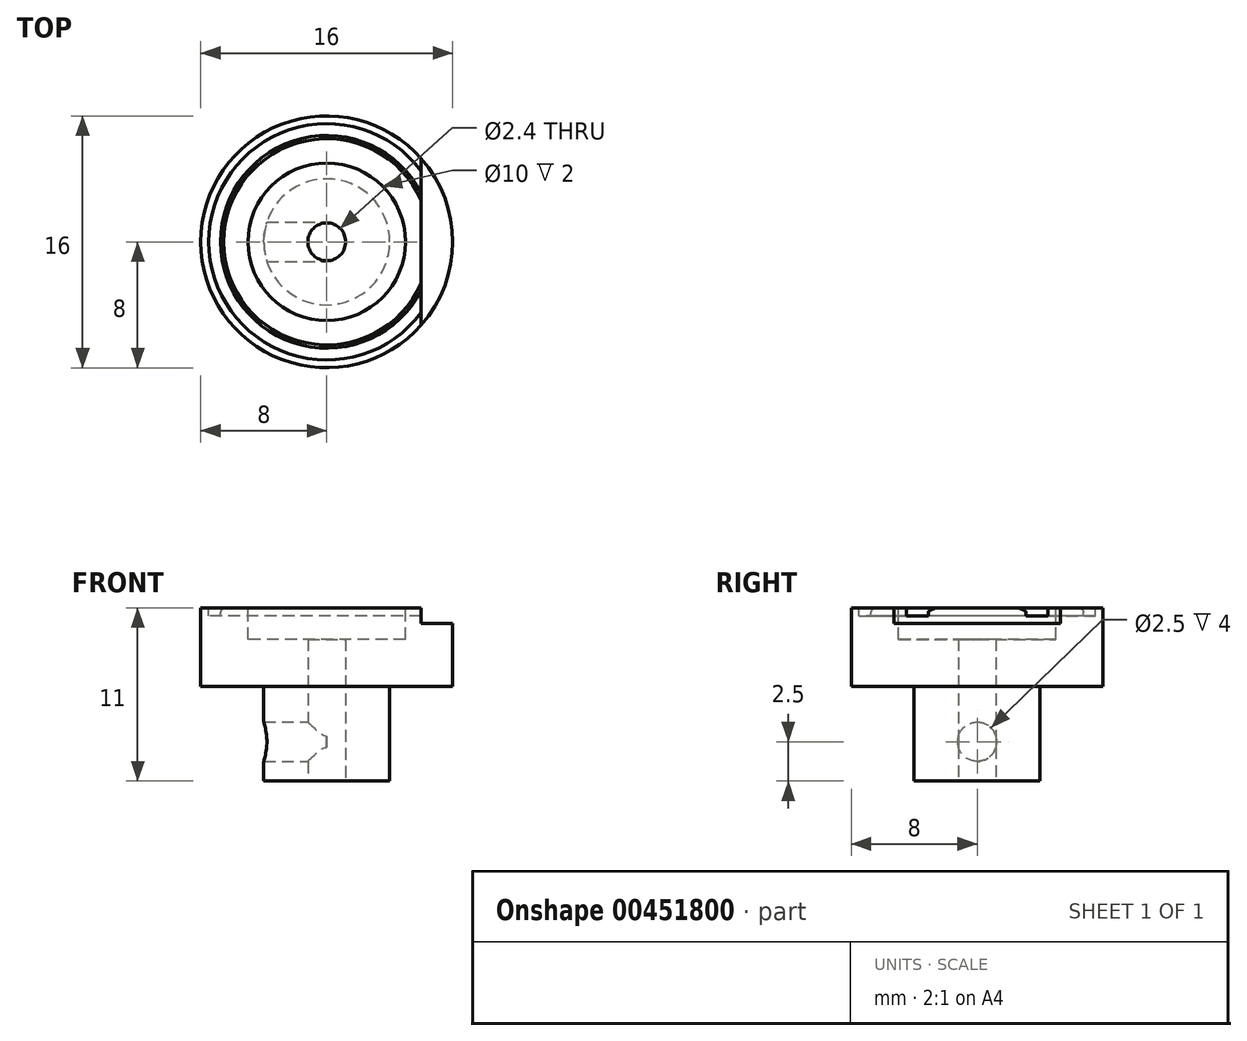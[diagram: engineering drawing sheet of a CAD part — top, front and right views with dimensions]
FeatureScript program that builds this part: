
annotation { "Feature Type Name" : "Feature", "Feature Type Description" : "" }
export const myFeature = defineFeature(function(context is Context, id is Id, definition is map)
    precondition{}
    {
        {
            var Q0;
            Q0=qCreatedBy(makeId("Top.planeOp"),FACE);
            var sketch = newSketch(context, id + "F0", { "sketchPlane" : qUnion([Q0])});
            skCircle(sketch, "E0", {"center": v(0, 0) * mm, "radius": 8 * mm});
            skSolve(sketch);
        }
        {
            var Q0;
            Q0=qSketchRegion(id+"F0",true);
            extrude(context, id + "F1", {"entities" : qUnion([Q0]), "depth" : 5 * mm});
        }
        {
            var Q0;
            Q0=makeQuery(id+"F1.opExtrude","CAP_FACE",FACE,{"disambiguationData":[OSD([sQuery(id+"F0.wireOp",EDGE,"E0")])],"isStart":true});
            var sketch = newSketch(context, id + "F2", { "sketchPlane" : qUnion([Q0])});
            skCircle(sketch, "E1", {"center": v(0, 0) * mm, "radius": 4 * mm});
            skSolve(sketch);
        }
        {
            var Q0;
            Q0=qSketchRegion(id+"F2",true);
            extrude(context, id + "F3", {"entities" : qUnion([Q0]), "operationType" : NewBodyOperationType.ADD, "depth" : 6 * mm});
        }
        {
            var Q0;
            Q0=makeQuery(id+"F3.opExtrude","CAP_FACE",FACE,{"disambiguationData":[OSD([sQuery(id+"F2.wireOp",EDGE,"E1")])],"isStart":false});
            var sketch = newSketch(context, id + "F4", { "sketchPlane" : qUnion([Q0])});
            skCircle(sketch, "E2", {"center": v(0, 0) * mm, "radius": 1.2 * mm});
            skSolve(sketch);
        }
        {
            var Q0;
            Q0=qSketchRegion(id+"F4",true);
            extrude(context, id + "F5", {"entities" : qUnion([Q0]), "operationType" : NewBodyOperationType.REMOVE, "oppositeDirection" : true, "depth" : 9 * mm});
        }
        {
            var Q0;
            Q0=makeQuery(id+"F1.opExtrude","CAP_FACE",FACE,{"disambiguationData":[OSD([sQuery(id+"F0.wireOp",EDGE,"E0")])],"isStart":false});
            var sketch = newSketch(context, id + "F6", { "sketchPlane" : qUnion([Q0])});
            skCircle(sketch, "E3", {"center": v(0, 0) * mm, "radius": 5 * mm});
            skSolve(sketch);
        }
        {
            var Q0;
            Q0=qSketchRegion(id+"F6",true);
            extrude(context, id + "F7", {"entities" : qUnion([Q0]), "operationType" : NewBodyOperationType.REMOVE, "oppositeDirection" : true, "depth" : 2 * mm});
        }
        {
            var Q0;
            Q0=makeQuery(id+"F1.opExtrude","CAP_FACE",FACE,{"disambiguationData":[OSD([sQuery(id+"F0.wireOp",EDGE,"E0")])],"isStart":false});
            var sketch = newSketch(context, id + "F8", { "sketchPlane" : qUnion([Q0])});
            skCircle(sketch, "E4", {"center": v(0, 0) * mm, "radius": 7.5 * mm});
            skCircle(sketch, "E5", {"center": v(0, 0) * mm, "radius": 6.75 * mm});
            skSolve(sketch);
        }
        {
            var Q0;
            Q0=makeQuery(id+"F8.imprint","IMPRINT",FACE,{"disambiguationData":[TD([[makeQuery(id+"F8.imprint","IMPRINT",EDGE,{"derivedFrom":sQuery(id+"F8.wireOp",EDGE,"E4")}),1.0]])]});
            extrude(context, id + "F9", {"entities" : qUnion([Q0]), "operationType" : NewBodyOperationType.REMOVE, "oppositeDirection" : true, "depth" : 0.5 * mm});
        }
        {
            var Q0;
            Q0=makeQuery(id+"F9.boolean.opBoolean","COPY",EDGE,{"derivedFrom":makeQuery(id+"F9.opExtrude","CAP_EDGE",EDGE,{"disambiguationData":[OSD([sQuery(id+"F8.wireOp",EDGE,"E5")])],"isStart":true})});
            chamfer(context, id + "F10", {"entities" : qUnion([Q0]), "width" : 0.2 * mm, "tangentPropagation" : true});
        }
        {
            var Q0;
            {var subQ0=sQuery(id+"F8.wireOp",EDGE,"E5");Q0=makeQuery(id+"F10.opChamfer","BLEND_EDGE",EDGE,{"blendedFrom":[makeQuery(id+"F9.boolean.opBoolean","COPY",EDGE,{"derivedFrom":makeQuery(id+"F9.opExtrude","CAP_EDGE",EDGE,{"disambiguationData":[OSD([subQ0])],"isStart":true})}),makeQuery(id+"F9.boolean.opBoolean","COPY",FACE,{"derivedFrom":makeQuery(id+"F9.opExtrude","SWEPT_FACE",FACE,{"disambiguationData":[OSD([subQ0])]})})],"blendedInto":[makeQuery(id+"F9.boolean.opBoolean","COPY",FACE,{"derivedFrom":makeQuery(id+"F9.opExtrude","SWEPT_FACE",FACE,{"disambiguationData":[OSD([subQ0])]})})]});}
            var Q1;
            Q1=makeQuery(id+"F5.boolean.opBoolean","COPY",EDGE,{"derivedFrom":makeQuery(id+"F5.opExtrude","CAP_EDGE",EDGE,{"disambiguationData":[OSD([sQuery(id+"F4.wireOp",EDGE,"E2")])],"isStart":false})});
            var Q2;
            Q2=makeQuery(id+"F5.boolean.opBoolean","COPY",EDGE,{"derivedFrom":makeQuery(id+"F5.opExtrude","CAP_EDGE",EDGE,{"disambiguationData":[OSD([sQuery(id+"F4.wireOp",EDGE,"E2")])],"isStart":true})});
            fillet(context, id + "F11", {"entities" : qUnion([Q0, Q1, Q2]), "radius" : 0.2 * mm, "tangentPropagation" : true, "allowEdgeOverflow" : false});
        }
        {
            var Q0;
            Q0=qCreatedBy(makeId("Top.planeOp"),FACE);
            cPlane(context, id + "F12", {"entities" : qUnion([Q0]), "cplaneType" : CPlaneType.OFFSET, "offset" : 5 * mm, "width" : 150 * mm, "height" : 150 * mm});
        }
        {
            var Q0;
            Q0=qCreatedBy(makeId("Right.planeOp"),FACE);
            var sketch = newSketch(context, id + "F13", { "sketchPlane" : qUnion([Q0])});
            skPoint(sketch, "E6", {"position": v(0, -3.5) * mm});
            skCircle(sketch, "E7", {"center": v(0, -3.5) * mm, "radius": 1.25 * mm});
            skSolve(sketch);
        }
        {
            var Q0;
            Q0=qSketchRegion(id+"F13",true);
            extrude(context, id + "F14", {"entities" : qUnion([Q0]), "operationType" : NewBodyOperationType.REMOVE, "oppositeDirection" : true, "depth" : 4.5 * mm});
        }
        {
            var Q0;
            Q0=qCreatedBy(id+"F12.planeOp",FACE);
            var sketch = newSketch(context, id + "F15", { "sketchPlane" : qUnion([Q0])});
            skLineSegment(sketch, "E8.bottom", {"start": v(6, 5.63) * mm, "end": v(8, 5.63) * mm});
            skLineSegment(sketch, "E8.top", {"start": v(6, -6.37) * mm, "end": v(8, -6.37) * mm});
            skLineSegment(sketch, "E8.left", {"start": v(6, 5.63) * mm, "end": v(6, -6.37) * mm});
            skLineSegment(sketch, "E8.right", {"start": v(8, 5.63) * mm, "end": v(8, -6.37) * mm});
            skSolve(sketch);
        }
        {
            var Q0;
            Q0=qSketchRegion(id+"F15",true);
            extrude(context, id + "F16", {"entities" : qUnion([Q0]), "operationType" : NewBodyOperationType.REMOVE, "oppositeDirection" : true, "depth" : 1 * mm, "offsetDistance" : 25 * mm});
        }
    });
